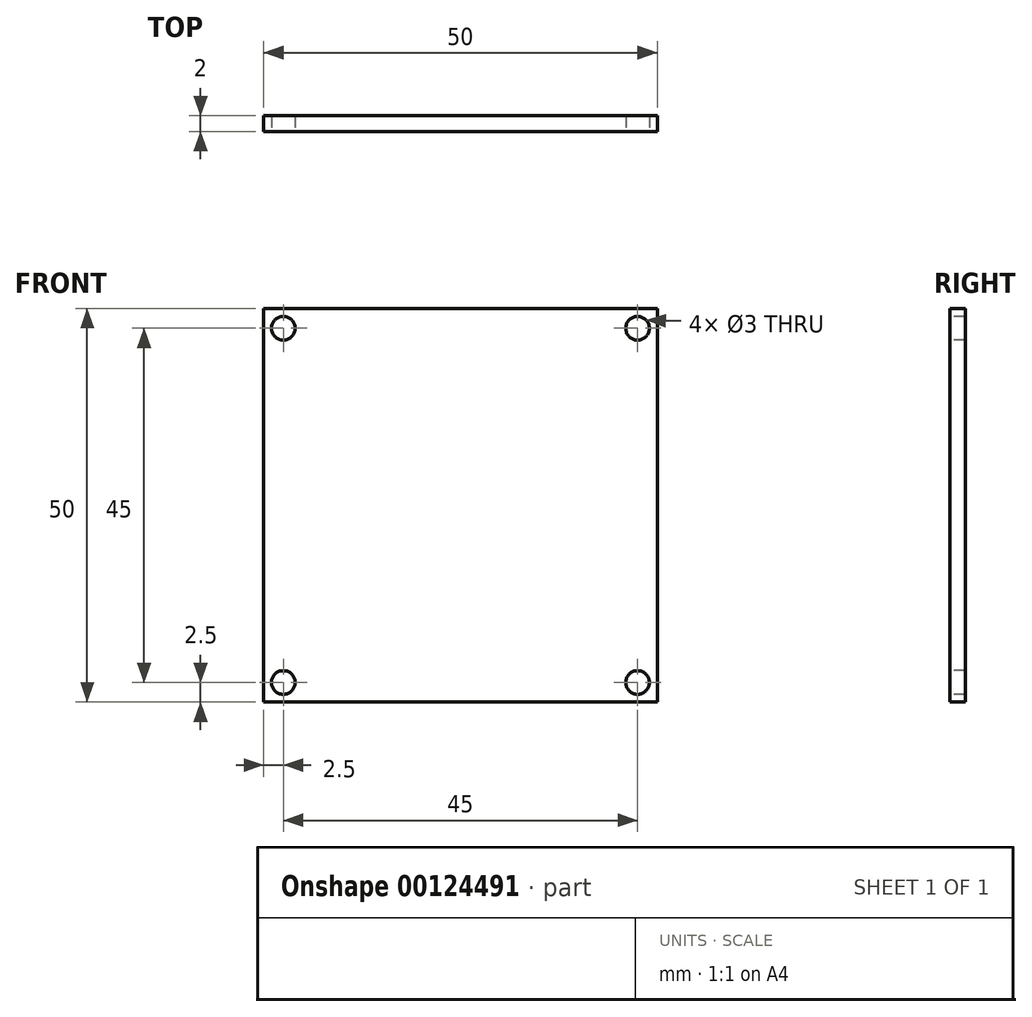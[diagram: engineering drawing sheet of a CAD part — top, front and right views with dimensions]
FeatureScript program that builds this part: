
annotation { "Feature Type Name" : "Feature", "Feature Type Description" : "" }
export const myFeature = defineFeature(function(context is Context, id is Id, definition is map)
    precondition{}
    {
        {
            var Q0;
            Q0=qCreatedBy(makeId("Front.planeOp"),FACE);
            var sketch = newSketch(context, id + "F0", { "sketchPlane" : qUnion([Q0])});
            skLineSegment(sketch, "E0.bottom", {"start": v(-25, 25) * mm, "end": v(25, 25) * mm});
            skLineSegment(sketch, "E0.top", {"start": v(-25, -25) * mm, "end": v(25, -25) * mm});
            skLineSegment(sketch, "E0.left", {"start": v(-25, 25) * mm, "end": v(-25, -25) * mm});
            skLineSegment(sketch, "E0.right", {"start": v(25, 25) * mm, "end": v(25, -25) * mm});
            skCircle(sketch, "E1", {"center": v(-22.5, 22.5) * mm, "radius": 1.5 * mm});
            skCircle(sketch, "E2", {"center": v(-22.5, -22.5) * mm, "radius": 1.5 * mm});
            skCircle(sketch, "E3", {"center": v(22.5, -22.5) * mm, "radius": 1.5 * mm});
            skCircle(sketch, "E4", {"center": v(22.5, 22.5) * mm, "radius": 1.5 * mm});
            skSolve(sketch);
        }
        {
            var Q0;
            Q0 = qSketchRegion(id + "F0", true);
            extrude(context, id + "F1", {"entities" : qUnion([Q0]), "oppositeDirection" : true, "depth" : 2 * mm});
        }
    });
